# Revit family: 6290 Series
name_source: partatom
category: Mechanical Equipment
revit_build: Autodesk Revit 2013 (Build: 20120221_2030(x64)
units: mm (PartAtom-declared; Revit-internal decimal feet)

## types (66) — shared parameters
Assembly Code = D2010900
Default Elevation = 0"
Description = Commercial Sewage Pumps
Discharge Height = 6"
Height = 21 3/16"
Hertz = 60
Impeller Type = Bronze Vortex
Installation Type = Floor Mounted
Insulation = Class B
Lead Wires Insulation = Class B
Length = 12 3/4"
Manufacturer = Zoeller
Masterformat Number = 33 36 16
Masterformat Title = Utility Septic Tank Effluent Pumps
Material = Cast Iron-Zoeller-Powder Coated Epoxy
Max. Stator Temp. = 266 °F
Max. Water Temp. = 130 °F
Min. Recommended Fluid Level = 10"
Moisture Sensor (Optional) = Requires a circuit in control panel
Motor Design Letter = NEMA B
Motor Shaft = 416 S.S.
Motor Thermal Shutoff (Single Phase Only) = Thermal Overload Sensors With Automatic Reset.
Motor Type = Submersible
O-Rings and Cover Gasket = Viton
Omniclass Table 23 Code = 23.60.30.21
Omniclass Table 23 Title = Pumps
Operation = Non-Automatic
Price = Prices may vary. Please consult Manufacturer Representative for most up-to-date price list.
Product Page URL = http://www.zoellerengprod.com
RPM = 3450
Service Factor = 1.15
Shaft Seal Lower (Options) = Silicon Carbide/Silicon Carbide
Shaft Seal Lower Standard = Silicon Carbide/Carbon
Shaft Seal Upper (Options) = Silicon Carbide/Carbon, Silicon Carbide/Silicon Carbide
Shaft Seal Upper Standard = Carbon/Ceramic
Shipping Weight = 93-96 lbs
Type SOW Power Cord Length = 300"
URL = http://www.zoellerengprod.com
Warranty Information = 36 Months (Limited)
Waste Connection = Yes
Width = 8"

## per-type parameters (varying)
| type | Apparent Load | Discharge Diameter | Discharge Radius | Flow 6292, 6294, 6295 @ 5', 6293 @ 15' | Full Load Amps | Locked Rotor Amps (Voltage Dependant) | Maximum Head | Minimum Head | Model | Motor | Phase | Type | Voltage |
| 6292-2" 115V 1Ph | 1725 VA | 2" NPT | 1" | 140 GPM | 15 A | 52.2 | 504" | 60" | 6292-2" | 1/2 HP | 1 | Permanent Split Capacitor | 115 V |
| 6292-2" 200V 1Ph | 1760 VA | 2" NPT | 1" | 140 GPM | 9 A | 19.8 | 504" | 60" | 6292-2" | 1/2 HP | 1 | Permanent Split Capacitor | 200 V |
| 6292-2" 208V 1Ph | 1830 VA | 2" NPT | 1" | 140 GPM | 9 A | 19.8 | 504" | 60" | 6292-2" | 1/2 HP | 1 | Permanent Split Capacitor | 208 V |
| 6292-2" 230V 1Ph | 1725 VA | 2" NPT | 1" | 140 GPM | 8 A | 15.1 | 504" | 60" | 6292-2" | 1/2 HP | 1 | Permanent Split Capacitor | 230 V |
| 6292-2" 200V 3Ph | 1280 VA | 2" NPT | 1" | 140 GPM | 6 A | 23.6 | 504" | 60" | 6292-2" | 1/2 HP | 3 | 3 Phase | 200 V |
| 6292-2" 208V 3Ph | 1331 VA | 2" NPT | 1" | 140 GPM | 6 A | 23.6 | 504" | 60" | 6292-2" | 1/2 HP | 3 | 3 Phase | 208 V |
| 6292-2" 230V 3Ph | 1196 VA | 2" NPT | 1" | 140 GPM | 5 A | 24.0 | 504" | 60" | 6292-2" | 1/2 HP | 3 | 3 Phase | 230 V |
| 6292-2" 460V 3Ph | 1334 VA | 2" NPT | 1" | 140 GPM | 3 A | 12.0 | 504" | 60" | 6292-2" | 1/2 HP | 3 | 3 Phase | 460 V |
| 6292-2" 575V 3Ph | 1380 VA | 2" NPT | 1" | 140 GPM | 2 A | 11.3 | 504" | 60" | 6292-2" | 1/2 HP | 3 | 3 Phase | 575 V |
| 6292-3" 115V 1Ph | 1725 VA | 3" NPT | 1 1/2" | 140 GPM | 15 A | 52.2 | 504" | 60" | 6292-3" | 1/2 HP | 1 | Permanent Split Capacitor | 115 V |
| 6292-3" 200V 1Ph | 1760 VA | 3" NPT | 1 1/2" | 140 GPM | 9 A | 19.8 | 504" | 60" | 6292-3" | 1/2 HP | 1 | Permanent Split Capacitor | 200 V |
| 6292-3" 208V 1Ph | 1830 VA | 3" NPT | 1 1/2" | 140 GPM | 9 A | 19.8 | 504" | 60" | 6292-3" | 1/2 HP | 1 | Permanent Split Capacitor | 208 V |
| 6292-3" 230V 1Ph | 1725 VA | 3" NPT | 1 1/2" | 140 GPM | 8 A | 15.1 | 504" | 60" | 6292-3" | 1/2 HP | 1 | Permanent Split Capacitor | 230 V |
| 6292-3" 200V 3Ph | 1280 VA | 3" NPT | 1 1/2" | 140 GPM | 6 A | 23.6 | 504" | 60" | 6292-3" | 1/2 HP | 3 | 3 Phase | 200 V |
| 6292-3" 208V 3Ph | 1331 VA | 3" NPT | 1 1/2" | 140 GPM | 6 A | 23.6 | 504" | 60" | 6292-3" | 1/2 HP | 3 | 3 Phase | 208 V |
| 6292-3" 230V 3Ph | 1196 VA | 3" NPT | 1 1/2" | 140 GPM | 5 A | 24.0 | 504" | 60" | 6292-3" | 1/2 HP | 3 | 3 Phase | 230 V |
| 6292-3" 460V 3Ph | 1334 VA | 3" NPT | 1 1/2" | 140 GPM | 3 A | 12.0 | 504" | 60" | 6292-3" | 1/2 HP | 3 | 3 Phase | 460 V |
| 6292-3" 575V 3Ph | 1380 VA | 3" NPT | 1 1/2" | 140 GPM | 2 A | 11.3 | 504" | 60" | 6292-3" | 1/2 HP | 3 | 3 Phase | 575 V |
| 6293-2" 200V 1Ph | 2400 VA | 2" NPT | 1" | 118 GPM | 12 A | 34.0 | 600" | 180" | 6293-2" | 1 HP | 1 | Permanent Split Capacitor | 200 V |
| 6293-2" 208V 1Ph | 2496 VA | 2" NPT | 1" | 118 GPM | 12 A | 34.0 | 600" | 180" | 6293-2" | 1 HP | 1 | Permanent Split Capacitor | 208 V |
| 6293-2" 230V 1Ph | 2346 VA | 2" NPT | 1" | 118 GPM | 10 A | 31.0 | 600" | 180" | 6293-2" | 1 HP | 1 | Permanent Split Capacitor | 230 V |
| 6293-2" 200V 3Ph | 1640 VA | 2" NPT | 1" | 118 GPM | 8 A | 30.0 | 600" | 180" | 6293-2" | 1 HP | 3 | 3 Phase | 200 V |
| 6293-2" 208V 3Ph | 1706 VA | 2" NPT | 1" | 118 GPM | 8 A | 30.0 | 600" | 180" | 6293-2" | 1 HP | 3 | 3 Phase | 208 V |
| 6293-2" 230V 3Ph | 1748 VA | 2" NPT | 1" | 118 GPM | 8 A | 27.0 | 600" | 180" | 6293-2" | 1 HP | 3 | 3 Phase | 230 V |
| 6293-2" 460V 3Ph | 1840 VA | 2" NPT | 1" | 118 GPM | 4 A | 14.0 | 600" | 180" | 6293-2" | 1 HP | 3 | 3 Phase | 460 V |
| 6293-2" 575V 3Ph | 1898 VA | 2" NPT | 1" | 118 GPM | 3 A | 12.0 | 600" | 180" | 6293-2" | 1 HP | 3 | 3 Phase | 575 V |
| 6293-3" 200V 1Ph | 2400 VA | 3" NPT | 1 1/2" | 118 GPM | 12 A | 34.0 | 600" | 180" | 6293-3" | 1 HP | 1 | Permanent Split Capacitor | 200 V |
| 6293-3" 208V 1Ph | 2496 VA | 3" NPT | 1 1/2" | 118 GPM | 12 A | 34.0 | 600" | 180" | 6293-3" | 1 HP | 1 | Permanent Split Capacitor | 208 V |
| 6293-3" 230V 1Ph | 2346 VA | 3" NPT | 1 1/2" | 118 GPM | 10 A | 31.0 | 600" | 180" | 6293-3" | 1 HP | 1 | Permanent Split Capacitor | 230 V |
| 6293-3" 200V 3Ph | 1640 VA | 3" NPT | 1 1/2" | 118 GPM | 8 A | 30.0 | 600" | 180" | 6293-3" | 1 HP | 3 | 3 Phase | 200 V |
| 6293-3" 208V 3Ph | 1706 VA | 3" NPT | 1 1/2" | 118 GPM | 8 A | 30.0 | 600" | 180" | 6293-3" | 1 HP | 3 | 3 Phase | 208 V |
| 6293-3" 230V 3Ph | 1748 VA | 3" NPT | 1 1/2" | 118 GPM | 8 A | 27.0 | 600" | 180" | 6293-3" | 1 HP | 3 | 3 Phase | 230 V |
| 6293-3" 460V 3Ph | 1840 VA | 3" NPT | 1 1/2" | 118 GPM | 4 A | 14.0 | 600" | 180" | 6293-3" | 1 HP | 3 | 3 Phase | 460 V |
| 6293-3" 575V 3Ph | 1898 VA | 3" NPT | 1 1/2" | 118 GPM | 3 A | 12.0 | 600" | 180" | 6293-3" | 1 HP | 3 | 3 Phase | 575 V |
| 6294-2" 200V 1Ph | 3560 VA | 2" NPT | 1" | 196 GPM | 18 A | 48.3 | 744" | 60" | 6294-2" | 1-1/2 HP | 1 | Permanent Split Capacitor | 200 V |
| 6294-2" 208V 1Ph | 3702 VA | 2" NPT | 1" | 196 GPM | 18 A | 48.3 | 744" | 60" | 6294-2" | 1-1/2 HP | 1 | Permanent Split Capacitor | 208 V |
| 6294-2" 230V 1Ph | 3151 VA | 2" NPT | 1" | 196 GPM | 14 A | 38.0 | 744" | 60" | 6294-2" | 1-1/2 HP | 1 | Permanent Split Capacitor | 230 V |
| 6294-2" 200V 3Ph | 2160 VA | 2" NPT | 1" | 196 GPM | 11 A | 42.0 | 744" | 60" | 6294-2" | 1-1/2 HP | 3 | 3 Phase | 200 V |
| 6294-2" 208V 3Ph | 2246 VA | 2" NPT | 1" | 196 GPM | 11 A | 42.0 | 744" | 60" | 6294-2" | 1-1/2 HP | 3 | 3 Phase | 208 V |
| 6294-2" 230V 3Ph | 2185 VA | 2" NPT | 1" | 196 GPM | 10 A | 35.0 | 744" | 60" | 6294-2" | 1-1/2 HP | 3 | 3 Phase | 230 V |
| 6294-2" 460V 3Ph | 2208 VA | 2" NPT | 1" | 196 GPM | 5 A | 18.0 | 744" | 60" | 6294-2" | 1-1/2 HP | 3 | 3 Phase | 460 V |
| 6294-2" 575V 3Ph | 2185 VA | 2" NPT | 1" | 196 GPM | 4 A | 18.0 | 744" | 60" | 6294-2" | 1-1/2 HP | 3 | 3 Phase | 575 V |
| 6294-3" 200V 1Ph | 3560 VA | 3" NPT | 1 1/2" | 196 GPM | 18 A | 48.3 | 744" | 60" | 6294-3" | 1-1/2 HP | 1 | Permanent Split Capacitor | 200 V |
| 6294-3" 208V 1Ph | 3702 VA | 3" NPT | 1 1/2" | 196 GPM | 18 A | 48.3 | 744" | 60" | 6294-3" | 1-1/2 HP | 1 | Permanent Split Capacitor | 208 V |
| 6294-3" 230V 1Ph | 3151 VA | 3" NPT | 1 1/2" | 196 GPM | 14 A | 38.0 | 744" | 60" | 6294-3" | 1-1/2 HP | 1 | Permanent Split Capacitor | 230 V |
| 6294-3" 200V 3Ph | 2160 VA | 3" NPT | 1 1/2" | 196 GPM | 11 A | 42.0 | 744" | 60" | 6294-3" | 1-1/2 HP | 3 | 3 Phase | 200 V |
| 6294-3" 208V 3Ph | 2246 VA | 3" NPT | 1 1/2" | 196 GPM | 11 A | 42.0 | 744" | 60" | 6294-3" | 1-1/2 HP | 3 | 3 Phase | 208 V |
| 6294-3" 230V 3Ph | 2185 VA | 3" NPT | 1 1/2" | 196 GPM | 10 A | 35.0 | 744" | 60" | 6294-3" | 1-1/2 HP | 3 | 3 Phase | 230 V |
| 6294-3" 460V 3Ph | 2208 VA | 3" NPT | 1 1/2" | 196 GPM | 5 A | 18.0 | 744" | 60" | 6294-3" | 1-1/2 HP | 3 | 3 Phase | 460 V |
| 6294-3" 575V 3Ph | 2185 VA | 3" NPT | 1 1/2" | 196 GPM | 4 A | 18.0 | 744" | 60" | 6294-3" | 1-1/2 HP | 3 | 3 Phase | 575 V |
| 6295-2" 200V 1Ph | 4100 VA | 2" NPT | 1" | 214 GPM | 21 A | 48.3 | 900" | 60" | 6295-2" | 2 HP | 1 | Permanent Split Capacitor | 200 V |
| 6295-2" 208V 1Ph | 4264 VA | 2" NPT | 1" | 214 GPM | 21 A | 48.3 | 900" | 60" | 6295-2" | 2 HP | 1 | Permanent Split Capacitor | 208 V |
| 6295-2" 230V 1Ph | 3933 VA | 2" NPT | 1" | 214 GPM | 17 A | 38.0 | 900" | 60" | 6295-2" | 2 HP | 1 | Permanent Split Capacitor | 230 V |
| 6295-2" 200V 3Ph | 2860 VA | 2" NPT | 1" | 214 GPM | 14 A | 42.0 | 900" | 60" | 6295-2" | 2 HP | 3 | 3 Phase | 200 V |
| 6295-2" 208V 3Ph | 2974 VA | 2" NPT | 1" | 214 GPM | 14 A | 42.0 | 900" | 60" | 6295-2" | 2 HP | 3 | 3 Phase | 208 V |
| 6295-2" 230V 3Ph | 2806 VA | 2" NPT | 1" | 214 GPM | 12 A | 35.0 | 900" | 60" | 6295-2" | 2 HP | 3 | 3 Phase | 230 V |
| 6295-2" 460V 3Ph | 2806 VA | 2" NPT | 1" | 214 GPM | 6 A | 18.0 | 900" | 60" | 6295-2" | 2 HP | 3 | 3 Phase | 460 V |
| 6295-2" 575V 3Ph | 2818 VA | 2" NPT | 1" | 214 GPM | 5 A | 18.0 | 900" | 60" | 6295-2" | 2 HP | 3 | 3 Phase | 575 V |
| 6295-3" 200V 1Ph | 4100 VA | 3" NPT | 1 1/2" | 214 GPM | 21 A | 48.3 | 900" | 60" | 6295-3" | 2 HP | 1 | Permanent Split Capacitor | 200 V |
| 6295-3" 208V 1Ph | 4264 VA | 3" NPT | 1 1/2" | 214 GPM | 21 A | 48.3 | 900" | 60" | 6295-3" | 2 HP | 1 | Permanent Split Capacitor | 208 V |
| 6295-3" 230V 1Ph | 3933 VA | 3" NPT | 1 1/2" | 214 GPM | 17 A | 38.0 | 900" | 60" | 6295-3" | 2 HP | 1 | Permanent Split Capacitor | 230 V |
| 6295-3" 200V 3Ph | 2860 VA | 3" NPT | 1 1/2" | 214 GPM | 14 A | 42.0 | 900" | 60" | 6295-3" | 2 HP | 3 | 3 Phase | 200 V |
| 6295-3" 208V 3Ph | 2974 VA | 3" NPT | 1 1/2" | 214 GPM | 14 A | 42.0 | 900" | 60" | 6295-3" | 2 HP | 3 | 3 Phase | 208 V |
| 6295-3" 230V 3Ph | 2806 VA | 3" NPT | 1 1/2" | 214 GPM | 12 A | 35.0 | 900" | 60" | 6295-3" | 2 HP | 3 | 3 Phase | 230 V |
| 6295-3" 460V 3Ph | 2806 VA | 3" NPT | 1 1/2" | 214 GPM | 6 A | 18.0 | 900" | 60" | 6295-3" | 2 HP | 3 | 3 Phase | 460 V |
| 6295-3" 575V 3Ph | 2818 VA | 3" NPT | 1 1/2" | 214 GPM | 5 A | 18.0 | 900" | 60" | 6295-3" | 2 HP | 3 | 3 Phase | 575 V |

## geometry (parser evidence)
native form markers: Blend x6, Sweep x3
no freeform markers — native parametric forms only
